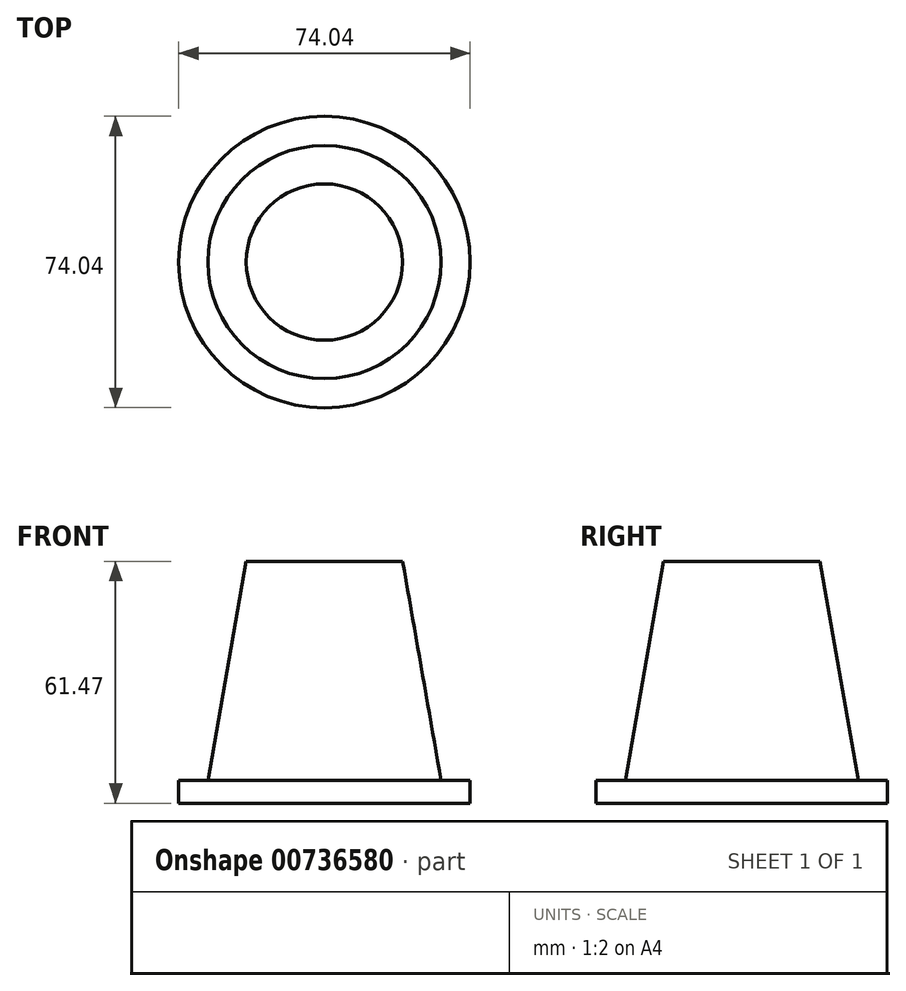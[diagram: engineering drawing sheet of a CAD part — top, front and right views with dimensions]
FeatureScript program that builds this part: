
annotation { "Feature Type Name" : "Feature", "Feature Type Description" : "" }
export const myFeature = defineFeature(function(context is Context, id is Id, definition is map)
    precondition{}
    {
        {
            var Q0;
            Q0=qCreatedBy(makeId("Top.planeOp"),FACE);
            var sketch = newSketch(context, id + "F0", { "sketchPlane" : qUnion([Q0])});
            skCircle(sketch, "E0", {"center": v(0, 0) * mm, "radius": 37.02 * mm});
            skSolve(sketch);
        }
        {
            var Q0;
            Q0 = qSketchRegion(id + "F0", true);
            extrude(context, id + "F1", {"entities" : qUnion([Q0]), "depth" : 5.84 * mm, "offsetDistance" : 25.4 * mm});
        }
        {
            var Q0;
            Q0=makeQuery(id+"F1.opExtrude","CAP_FACE",FACE,{"disambiguationData":[OSD([sQuery(id+"F0.wireOp",EDGE,"E0")])],"isStart":false});
            var sketch = newSketch(context, id + "F2", { "sketchPlane" : qUnion([Q0])});
            skCircle(sketch, "E1", {"center": v(0, 0) * mm, "radius": 29.61 * mm});
            skSolve(sketch);
        }
        {
            var Q0;
            Q0=qCreatedBy(makeId("Top.planeOp"),FACE);
            cPlane(context, id + "F3", {"entities" : qUnion([Q0]), "cplaneType" : CPlaneType.OFFSET, "offset" : 61.47 * mm, "width" : 152.4 * mm, "height" : 152.4 * mm});
        }
        {
            var Q0;
            Q0=qCreatedBy(id+"F3.planeOp",FACE);
            var sketch = newSketch(context, id + "F4", { "sketchPlane" : qUnion([Q0])});
            skCircle(sketch, "E2", {"center": v(0, 0) * mm, "radius": 19.87 * mm});
            skSolve(sketch);
        }
        {
            var Q0;
            Q0=makeQuery(id+"F4.imprint","IMPRINT",FACE,{"disambiguationData":[TD([[makeQuery(id+"F4.imprint","IMPRINT",EDGE,{"derivedFrom":sQuery(id+"F4.wireOp",EDGE,"E2")}),1.0]])]});
            var Q1;
            Q1=makeQuery(id+"F2.imprint","IMPRINT",FACE,{"disambiguationData":[TD([[makeQuery(id+"F2.imprint","IMPRINT",EDGE,{"derivedFrom":sQuery(id+"F2.wireOp",EDGE,"E1")}),1.0]])]});
            loft(context, id + "F5", {"sheetProfilesArray" : [{ "sheetProfileEntities" : qUnion([Q0]) }, { "sheetProfileEntities" : qUnion([Q1]) }]});
        }
    });
